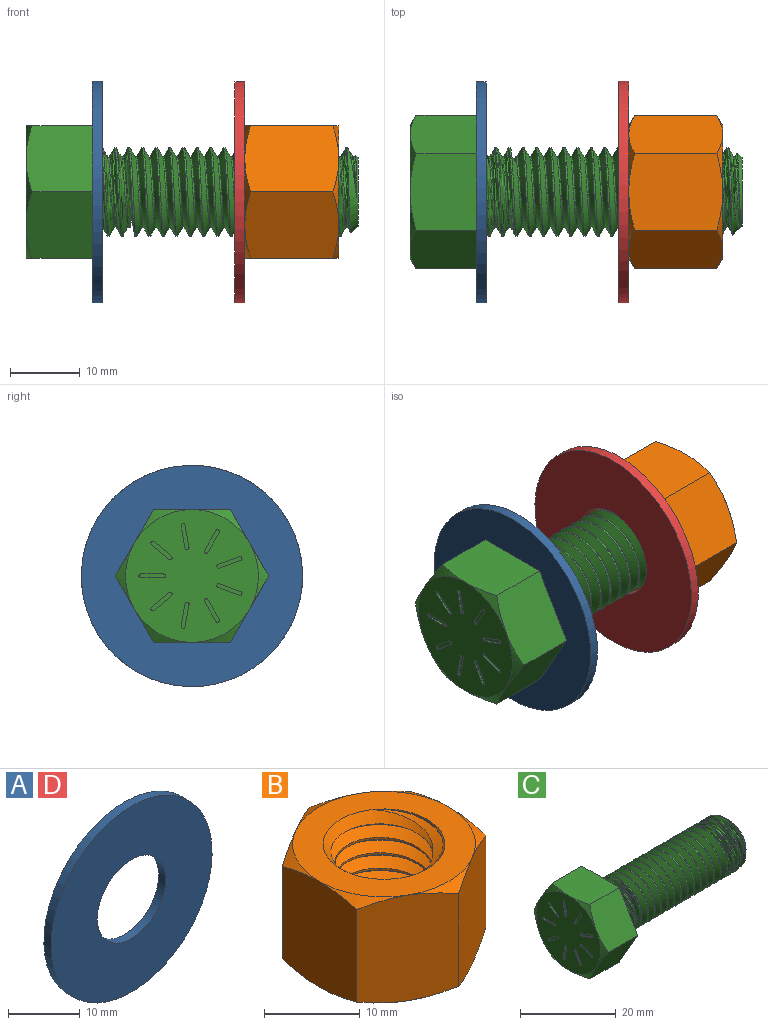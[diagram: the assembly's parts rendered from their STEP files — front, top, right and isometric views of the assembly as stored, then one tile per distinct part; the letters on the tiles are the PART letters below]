
ASSEMBLY  parts=4 mates=3
PART A: 4 faces, bbox 31.8x1.4x31.8 mm
  f0: cylinder r=15.88mm len=31.75mm, axis (0,-1,0), area 139.3mm2, adj f1,f2
  f1: plane 31.75x31.75mm, normal (0,1,0), area 648.9mm2, adj f0,f3
  f2: plane 31.75x31.75mm, normal (0,-1,0), area 648.9mm2, adj f0,f3
  f3: cylinder r=6.74mm len=13.49mm, axis (0,1,0), area 59.2mm2, adj f1,f2
PART B: 26 faces, bbox 22.9x22.9x15.9 mm
  f0: plane 19.05x19.05mm, normal (0,0,1), area 158.3mm2, adj f7,f12,f13,f14,f15,f16,f17,f18
  f1: plane 14.4x10.43mm, normal (-0.5,0.87,0), area 142mm2, adj f2,f6,f13,f18,f21,f22
  f2: plane 14.41x11.91mm, normal (-1,0,0), area 142mm2, adj f1,f3,f17,f18,f22,f23
  f3: plane 14.4x10.43mm, normal (-0.5,-0.87,0), area 142mm2, adj f2,f4,f16,f17,f23,f24
  f4: plane 14.4x10.43mm, normal (0.5,-0.87,0), area 142mm2, adj f3,f5,f15,f16,f24,f25
  f5: plane 14.41x11.91mm, normal (1,0,0), area 142mm2, adj f4,f6,f14,f15,f20,f25
  f6: plane 14.4x10.43mm, normal (0.5,0.87,0), area 142mm2, adj f1,f5,f13,f14,f20,f21
  f7: cylinder r=6.35mm len=13.49mm, axis (0,0,-1), area 69.4mm2, adj f0,f8,f9,f11
  f8: plane 19.05x19.05mm, normal (0,0,-1), area 158.3mm2, adj f7,f19,f20,f21,f22,f23,f24,f25
  f9: bspline ~14.23x12.7mm, area 330.8mm2, adj f7,f10,f12,f19
  f10: bspline ~11.58x10.69mm, area 43.7mm2, adj f9,f11,f12,f19
  f11: bspline ~14.41x13.35mm, area 330.8mm2, adj f7,f10,f12,f19
  f12: cone r=5.86mm half-angle=45deg, axis (0,0,1), area 33.1mm2, adj f0,f9,f10,f11
  f13: cone r=9.53mm half-angle=60deg, axis (0,0,-1), area 8.9mm2, adj f0,f1,f6
  f14: cone r=9.53mm half-angle=60deg, axis (0,0,-1), area 8.9mm2, adj f0,f5,f6
  f15: cone r=9.53mm half-angle=60deg, axis (0,0,-1), area 8.9mm2, adj f0,f4,f5
  f16: cone r=9.53mm half-angle=60deg, axis (0,0,-1), area 8.9mm2, adj f0,f3,f4
  f17: cone r=9.53mm half-angle=60deg, axis (0,0,-1), area 8.9mm2, adj f0,f2,f3
  f18: cone r=9.53mm half-angle=60deg, axis (0,0,-1), area 8.9mm2, adj f0,f1,f2
  f19: cone r=5.86mm half-angle=45deg, axis (0,0,-1), area 33.1mm2, adj f8,f9,f10,f11
  f20: cone r=9.53mm half-angle=60deg, axis (0,0,1), area 8.9mm2, adj f5,f6,f8
  f21: cone r=9.53mm half-angle=60deg, axis (0,0,1), area 8.9mm2, adj f1,f6,f8
  f22: cone r=9.53mm half-angle=60deg, axis (0,0,1), area 8.9mm2, adj f1,f2,f8
  f23: cone r=9.53mm half-angle=60deg, axis (0,0,1), area 8.9mm2, adj f2,f3,f8
  f24: cone r=9.53mm half-angle=60deg, axis (0,0,1), area 8.9mm2, adj f3,f4,f8
  f25: cone r=9.53mm half-angle=60deg, axis (0,0,1), area 8.9mm2, adj f4,f5,f8
PART C: 65 faces, bbox 48.9x22.9x22.9 mm
  f0: plane 11.91x10.43mm, normal (0,0,1), area 101.6mm2, adj f1,f5,f12,f13,f18
  f1: plane 10.43x10.43mm, normal (0,0.87,0.5), area 101.6mm2, adj f0,f2,f12,f17,f18
  f2: plane 10.43x10.43mm, normal (0,0.87,-0.5), area 101.6mm2, adj f1,f3,f12,f16,f17
  f3: plane 11.91x10.43mm, normal (0,0,-1), area 101.6mm2, adj f2,f4,f12,f15,f16
  f4: plane 10.43x10.43mm, normal (0,-0.87,-0.5), area 101.6mm2, adj f3,f5,f12,f14,f15
  f5: plane 10.43x10.43mm, normal (0,-0.87,0.5), area 101.6mm2, adj f0,f4,f12,f13,f14
  f6: cylinder r=6.35mm len=36.63mm, axis (1,0,0), area 197.3mm2, adj f7,f10,f11,f12
  f7: cone r=4.88mm half-angle=45deg, axis (-1,0,0), area 40mm2, adj f6,f8,f9,f10,f11
  f8: plane 9.77x9.77mm, normal (1,0,0), area 75mm2, adj f7
  f9: bspline ~38.54x10.69mm, area 151.2mm2, adj f7,f10,f11,f12
  f10: bspline ~38.83x13.35mm, area 1004.1mm2, adj f6,f7,f9,f12
  f11: bspline ~39.22x13.35mm, area 970.5mm2, adj f6,f7,f9,f12
  f12: plane 22.75x19.81mm, normal (1,0,0), area 211mm2, adj f0,f1,f2,f3,f4,f5,f6,f9
  f13: cone r=9.53mm half-angle=60deg, axis (1,0,0), area 8.9mm2, adj f0,f5,f19
  f14: cone r=9.53mm half-angle=60deg, axis (1,0,0), area 8.9mm2, adj f4,f5,f19
  f15: cone r=9.53mm half-angle=60deg, axis (1,0,0), area 8.9mm2, adj f3,f4,f19
  f16: cone r=9.53mm half-angle=60deg, axis (1,0,0), area 8.9mm2, adj f2,f3,f19
  f17: cone r=9.53mm half-angle=60deg, axis (1,0,0), area 8.9mm2, adj f1,f2,f19
  f18: cone r=9.53mm half-angle=60deg, axis (1,0,0), area 8.9mm2, adj f0,f1,f19
  f19: plane 19.05x19.05mm, normal (-1,0,0), area 266.1mm2, adj f13,f14,f15,f16,f17,f18,f20,f21
  f20: cylinder r=0.29mm len=0.57mm, axis (-1,0,0), area 0.2mm2, adj f19,f21,f23,f24
  f21: plane 3.24x0.25mm, normal (0,0,-1), area 0.8mm2, adj f19,f20,f22,f24
  f22: cylinder r=0.29mm len=0.57mm, axis (-1,0,0), area 0.2mm2, adj f19,f21,f23,f24
  f23: plane 3.24x0.25mm, normal (0,0,1), area 0.8mm2, adj f19,f20,f22,f24
  f24: plane 3.81x0.57mm, normal (-1,0,0), area 2.1mm2, adj f20,f21,f22,f23
  f25: cylinder r=0.29mm len=0.5mm, axis (-1,0,0), area 0.2mm2, adj f19,f26,f28,f29
  f26: plane 2.48x2.08mm, normal (0,0.64,-0.77), area 0.8mm2, adj f19,f25,f27,f29
  f27: cylinder r=0.29mm len=0.5mm, axis (-1,0,0), area 0.2mm2, adj f19,f26,f28,f29
  f28: plane 2.48x2.08mm, normal (0,-0.64,0.77), area 0.8mm2, adj f19,f25,f27,f29
  f29: plane 3.05x2.65mm, normal (-1,0,0), area 2.1mm2, adj f25,f26,f27,f28
  f30: cylinder r=0.29mm len=0.57mm, axis (-1,0,0), area 0.2mm2, adj f19,f31,f33,f34
  f31: plane 3.19x0.56mm, normal (0,0.98,-0.17), area 0.8mm2, adj f19,f30,f32,f34
  f32: cylinder r=0.29mm len=0.57mm, axis (-1,0,0), area 0.2mm2, adj f19,f31,f33,f34
  f33: plane 3.19x0.56mm, normal (0,-0.98,0.17), area 0.8mm2, adj f19,f30,f32,f34
  f34: plane 3.76x1.13mm, normal (-1,0,0), area 2.1mm2, adj f30,f31,f32,f33
  f35: cylinder r=0.29mm len=0.53mm, axis (-1,0,0), area 0.2mm2, adj f19,f36,f38,f39
  f36: plane 2.8x1.62mm, normal (0,0.87,0.5), area 0.8mm2, adj f19,f35,f37,f39
  f37: cylinder r=0.29mm len=0.53mm, axis (-1,0,0), area 0.2mm2, adj f19,f36,f38,f39
  f38: plane 2.8x1.62mm, normal (0,-0.87,-0.5), area 0.8mm2, adj f19,f35,f37,f39
  f39: plane 3.38x2.19mm, normal (-1,0,0), area 2.1mm2, adj f35,f36,f37,f38
  f40: cylinder r=0.29mm len=0.55mm, axis (-1,0,0), area 0.2mm2, adj f19,f41,f43,f44
  f41: plane 3.04x1.11mm, normal (0,0.34,0.94), area 0.8mm2, adj f19,f40,f42,f44
  f42: cylinder r=0.29mm len=0.55mm, axis (-1,0,0), area 0.2mm2, adj f19,f41,f43,f44
  f43: plane 3.04x1.11mm, normal (0,-0.34,-0.94), area 0.8mm2, adj f19,f40,f42,f44
  f44: plane 3.61x1.68mm, normal (-1,0,0), area 2.1mm2, adj f40,f41,f42,f43
  f45: cylinder r=0.29mm len=0.55mm, axis (-1,0,0), area 0.2mm2, adj f19,f46,f48,f49
  f46: plane 3.04x1.11mm, normal (0,-0.34,0.94), area 0.8mm2, adj f19,f45,f47,f49
  f47: cylinder r=0.29mm len=0.55mm, axis (-1,0,0), area 0.2mm2, adj f19,f46,f48,f49
  f48: plane 3.04x1.11mm, normal (0,0.34,-0.94), area 0.8mm2, adj f19,f45,f47,f49
  f49: plane 3.61x1.68mm, normal (-1,0,0), area 2.1mm2, adj f45,f46,f47,f48
  f50: cylinder r=0.29mm len=0.53mm, axis (-1,0,0), area 0.2mm2, adj f19,f51,f53,f54
  f51: plane 2.8x1.62mm, normal (0,-0.87,0.5), area 0.8mm2, adj f19,f50,f52,f54
  f52: cylinder r=0.29mm len=0.53mm, axis (-1,0,0), area 0.2mm2, adj f19,f51,f53,f54
  f53: plane 2.8x1.62mm, normal (0,0.87,-0.5), area 0.8mm2, adj f19,f50,f52,f54
  f54: plane 3.38x2.19mm, normal (-1,0,0), area 2.1mm2, adj f50,f51,f52,f53
  f55: cylinder r=0.29mm len=0.57mm, axis (-1,0,0), area 0.2mm2, adj f19,f56,f58,f59
  f56: plane 3.19x0.56mm, normal (0,-0.98,-0.17), area 0.8mm2, adj f19,f55,f57,f59
  f57: cylinder r=0.29mm len=0.57mm, axis (-1,0,0), area 0.2mm2, adj f19,f56,f58,f59
  f58: plane 3.19x0.56mm, normal (0,0.98,0.17), area 0.8mm2, adj f19,f55,f57,f59
  f59: plane 3.76x1.13mm, normal (-1,0,0), area 2.1mm2, adj f55,f56,f57,f58
  f60: cylinder r=0.29mm len=0.5mm, axis (-1,0,0), area 0.2mm2, adj f19,f61,f63,f64
  f61: plane 2.48x2.08mm, normal (0,-0.64,-0.77), area 0.8mm2, adj f19,f60,f62,f64
  f62: cylinder r=0.29mm len=0.5mm, axis (-1,0,0), area 0.2mm2, adj f19,f61,f63,f64
  f63: plane 2.48x2.08mm, normal (0,0.64,0.77), area 0.8mm2, adj f19,f60,f62,f64
  f64: plane 3.05x2.65mm, normal (-1,0,0), area 2.1mm2, adj f60,f61,f62,f63
PART D: same geometry as A
PLACE A rot(axis=(0.58,0.58,-0.58),120deg) t=(-13.9,1.94,2.58)mm
PLACE B rot(axis=(0.71,0,0.71),180deg) t=(14.69,1.94,2.58)mm
PLACE C t=(0.38,1.94,2.58)mm fixed
PLACE D rot(axis=(0.71,0.71,0),180deg) t=(6.54,1.94,2.58)mm
MATE fastened A.f0 <-> C.f6  axis (-1,0,0) through (-13.9,1.94,2.58)mm
MATE fastened B.f19 <-> D.f0  axis (-1,0,0) through (7.94,1.94,2.58)mm
MATE fastened D.f0 <-> A.f0  axis (-1,0,0) through (6.54,1.94,2.58)mm
